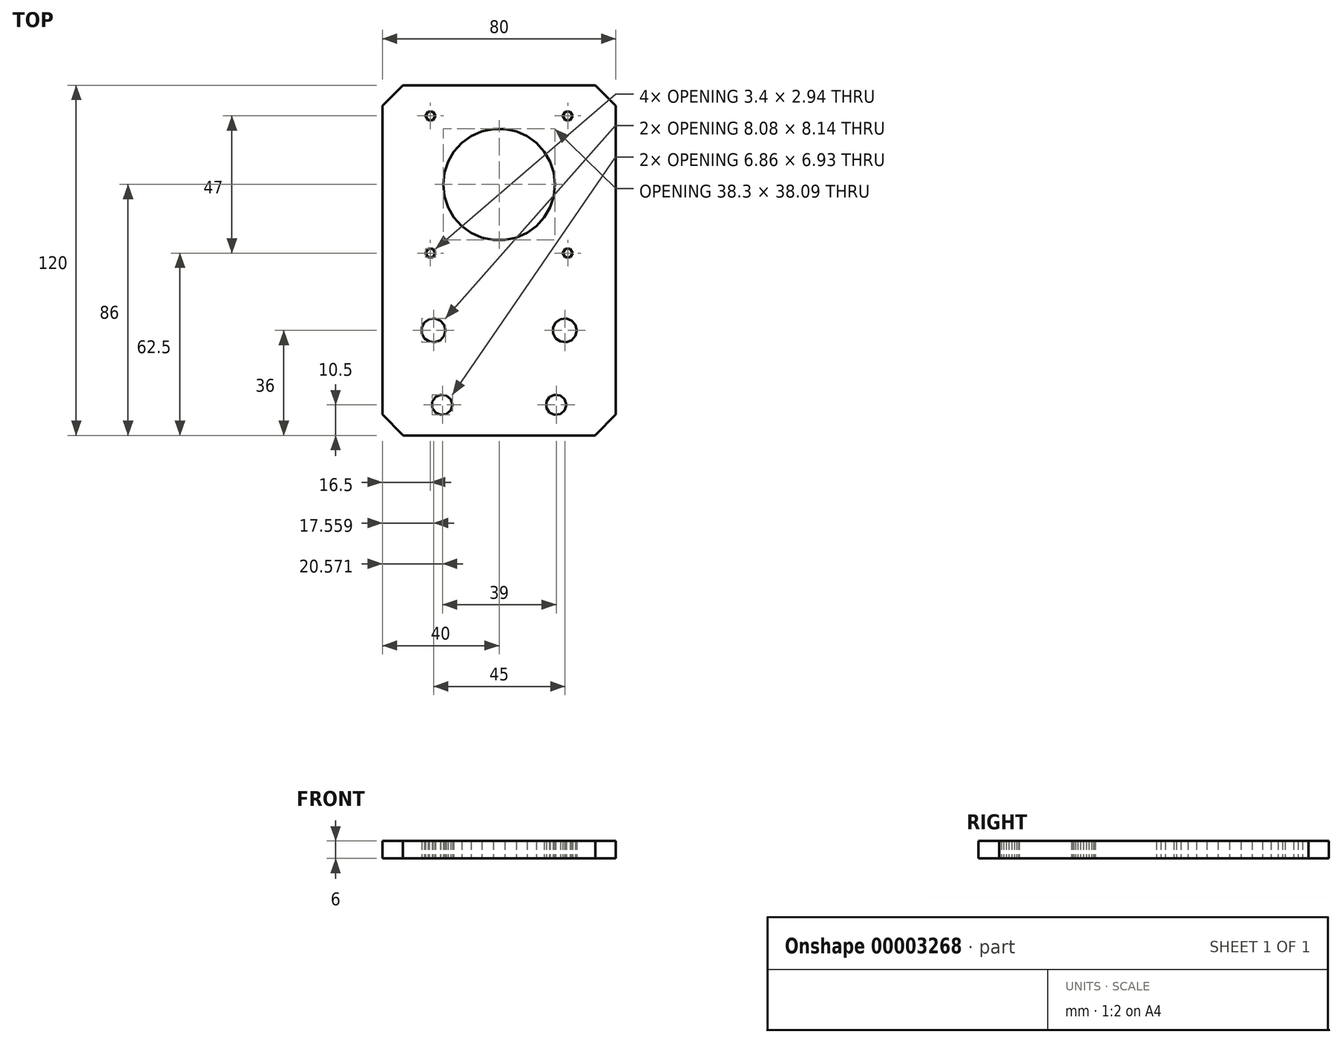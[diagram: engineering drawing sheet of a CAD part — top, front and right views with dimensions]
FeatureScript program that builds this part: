
annotation { "Feature Type Name" : "Feature", "Feature Type Description" : "" }
export const myFeature = defineFeature(function(context is Context, id is Id, definition is map)
    precondition{}
    {
        {
            var Q0;
            Q0=qCreatedBy(makeId("Top.planeOp"),FACE);
            var sketch = newSketch(context, id + "F0", { "sketchPlane" : qUnion([Q0])});
            skLineSegment(sketch, "E0", {"start": v(-40, -52.86) * mm, "end": v(-40, 53) * mm});
            skLineSegment(sketch, "E1", {"start": v(-40, 53) * mm, "end": v(-33, 60) * mm});
            skLineSegment(sketch, "E2", {"start": v(-33, 60) * mm, "end": v(33, 60) * mm});
            skLineSegment(sketch, "E3", {"start": v(33, 60) * mm, "end": v(40, 53) * mm});
            skLineSegment(sketch, "E4", {"start": v(40, 53) * mm, "end": v(40, -52.86) * mm});
            skLineSegment(sketch, "E5", {"start": v(40, -52.86) * mm, "end": v(32.93, -59.93) * mm});
            skLineSegment(sketch, "E6", {"start": v(32.93, -59.93) * mm, "end": v(33, -60) * mm});
            skLineSegment(sketch, "E7", {"start": v(33, -60) * mm, "end": v(-33, -60) * mm});
            skLineSegment(sketch, "E8", {"start": v(-33, -60) * mm, "end": v(-32.93, -59.93) * mm});
            skLineSegment(sketch, "E9", {"start": v(-32.93, -59.93) * mm, "end": v(-40, -52.86) * mm});
            skLineSegment(sketch, "E10", {"start": v(-26.48, -24.98) * mm, "end": v(-26.48, -23.02) * mm});
            skLineSegment(sketch, "E11", {"start": v(-26.48, -23.02) * mm, "end": v(-25.57, -21.28) * mm});
            skLineSegment(sketch, "E12", {"start": v(-25.57, -21.28) * mm, "end": v(-23.95, -20.17) * mm});
            skLineSegment(sketch, "E13", {"start": v(-23.95, -20.17) * mm, "end": v(-22, -19.93) * mm});
            skLineSegment(sketch, "E14", {"start": v(-22, -19.93) * mm, "end": v(-20.17, -20.63) * mm});
            skLineSegment(sketch, "E15", {"start": v(-20.17, -20.63) * mm, "end": v(-18.87, -22.1) * mm});
            skLineSegment(sketch, "E16", {"start": v(-18.87, -22.1) * mm, "end": v(-18.4, -24) * mm});
            skLineSegment(sketch, "E17", {"start": v(-18.4, -24) * mm, "end": v(-18.87, -25.9) * mm});
            skLineSegment(sketch, "E18", {"start": v(-18.87, -25.9) * mm, "end": v(-20.17, -27.37) * mm});
            skLineSegment(sketch, "E19", {"start": v(-20.17, -27.37) * mm, "end": v(-22, -28.07) * mm});
            skLineSegment(sketch, "E20", {"start": v(-22, -28.07) * mm, "end": v(-23.95, -27.83) * mm});
            skLineSegment(sketch, "E21", {"start": v(-23.95, -27.83) * mm, "end": v(-25.57, -26.72) * mm});
            skLineSegment(sketch, "E22", {"start": v(-25.57, -26.72) * mm, "end": v(-26.48, -24.98) * mm});
            skLineSegment(sketch, "E23", {"start": v(-25.2, 2.5) * mm, "end": v(-24.35, 3.97) * mm});
            skLineSegment(sketch, "E24", {"start": v(-24.35, 3.97) * mm, "end": v(-22.65, 3.97) * mm});
            skLineSegment(sketch, "E25", {"start": v(-22.65, 3.97) * mm, "end": v(-21.8, 2.5) * mm});
            skLineSegment(sketch, "E26", {"start": v(-21.8, 2.5) * mm, "end": v(-22.65, 1.03) * mm});
            skLineSegment(sketch, "E27", {"start": v(-22.65, 1.03) * mm, "end": v(-24.35, 1.03) * mm});
            skLineSegment(sketch, "E28", {"start": v(-24.35, 1.03) * mm, "end": v(-25.2, 2.5) * mm});
            skLineSegment(sketch, "E29", {"start": v(-25.2, 49.5) * mm, "end": v(-24.35, 50.97) * mm});
            skLineSegment(sketch, "E30", {"start": v(-24.35, 50.97) * mm, "end": v(-22.65, 50.97) * mm});
            skLineSegment(sketch, "E31", {"start": v(-22.65, 50.97) * mm, "end": v(-21.8, 49.5) * mm});
            skLineSegment(sketch, "E32", {"start": v(-21.8, 49.5) * mm, "end": v(-22.65, 48.03) * mm});
            skLineSegment(sketch, "E33", {"start": v(-22.65, 48.03) * mm, "end": v(-24.35, 48.03) * mm});
            skLineSegment(sketch, "E34", {"start": v(-24.35, 48.03) * mm, "end": v(-25.2, 49.5) * mm});
            skLineSegment(sketch, "E35", {"start": v(-22.86, -50.49) * mm, "end": v(-22.86, -48.51) * mm});
            skLineSegment(sketch, "E36", {"start": v(-22.86, -48.51) * mm, "end": v(-21.8, -46.86) * mm});
            skLineSegment(sketch, "E37", {"start": v(-21.8, -46.86) * mm, "end": v(-20, -46.04) * mm});
            skLineSegment(sketch, "E38", {"start": v(-20, -46.04) * mm, "end": v(-18.05, -46.32) * mm});
            skLineSegment(sketch, "E39", {"start": v(-18.05, -46.32) * mm, "end": v(-16.56, -47.6) * mm});
            skLineSegment(sketch, "E40", {"start": v(-16.56, -47.6) * mm, "end": v(-16, -49.5) * mm});
            skLineSegment(sketch, "E41", {"start": v(-16, -49.5) * mm, "end": v(-16.56, -51.4) * mm});
            skLineSegment(sketch, "E42", {"start": v(-16.56, -51.4) * mm, "end": v(-18.05, -52.68) * mm});
            skLineSegment(sketch, "E43", {"start": v(-18.05, -52.68) * mm, "end": v(-20, -52.96) * mm});
            skLineSegment(sketch, "E44", {"start": v(-20, -52.96) * mm, "end": v(-21.8, -52.15) * mm});
            skLineSegment(sketch, "E45", {"start": v(-21.8, -52.15) * mm, "end": v(-22.86, -50.49) * mm});
            skLineSegment(sketch, "E46", {"start": v(-19.15, 26) * mm, "end": v(-18.73, 29.98) * mm});
            skLineSegment(sketch, "E47", {"start": v(-18.73, 29.98) * mm, "end": v(-17.5, 33.79) * mm});
            skLineSegment(sketch, "E48", {"start": v(-17.5, 33.79) * mm, "end": v(-15.5, 37.26) * mm});
            skLineSegment(sketch, "E49", {"start": v(-15.5, 37.26) * mm, "end": v(-12.81, 40.23) * mm});
            skLineSegment(sketch, "E50", {"start": v(-12.81, 40.23) * mm, "end": v(-9.57, 42.58) * mm});
            skLineSegment(sketch, "E51", {"start": v(-9.57, 42.58) * mm, "end": v(-5.92, 44.21) * mm});
            skLineSegment(sketch, "E52", {"start": v(-5.92, 44.21) * mm, "end": v(-2, 45.05) * mm});
            skLineSegment(sketch, "E53", {"start": v(-2, 45.05) * mm, "end": v(2, 45.05) * mm});
            skLineSegment(sketch, "E54", {"start": v(2, 45.05) * mm, "end": v(5.92, 44.21) * mm});
            skLineSegment(sketch, "E55", {"start": v(5.92, 44.21) * mm, "end": v(9.57, 42.58) * mm});
            skLineSegment(sketch, "E56", {"start": v(9.57, 42.58) * mm, "end": v(12.81, 40.23) * mm});
            skLineSegment(sketch, "E57", {"start": v(12.81, 40.23) * mm, "end": v(15.5, 37.26) * mm});
            skLineSegment(sketch, "E58", {"start": v(15.5, 37.26) * mm, "end": v(17.5, 33.79) * mm});
            skLineSegment(sketch, "E59", {"start": v(17.5, 33.79) * mm, "end": v(18.73, 29.98) * mm});
            skLineSegment(sketch, "E60", {"start": v(18.73, 29.98) * mm, "end": v(19.15, 26) * mm});
            skLineSegment(sketch, "E61", {"start": v(19.15, 26) * mm, "end": v(18.73, 22.02) * mm});
            skLineSegment(sketch, "E62", {"start": v(18.73, 22.02) * mm, "end": v(17.5, 18.21) * mm});
            skLineSegment(sketch, "E63", {"start": v(17.5, 18.21) * mm, "end": v(15.5, 14.74) * mm});
            skLineSegment(sketch, "E64", {"start": v(15.5, 14.74) * mm, "end": v(12.81, 11.77) * mm});
            skLineSegment(sketch, "E65", {"start": v(12.81, 11.77) * mm, "end": v(9.57, 9.42) * mm});
            skLineSegment(sketch, "E66", {"start": v(9.57, 9.42) * mm, "end": v(5.92, 7.79) * mm});
            skLineSegment(sketch, "E67", {"start": v(5.92, 7.79) * mm, "end": v(2, 6.96) * mm});
            skLineSegment(sketch, "E68", {"start": v(2, 6.96) * mm, "end": v(-2, 6.96) * mm});
            skLineSegment(sketch, "E69", {"start": v(-2, 6.96) * mm, "end": v(-5.92, 7.79) * mm});
            skLineSegment(sketch, "E70", {"start": v(-5.92, 7.79) * mm, "end": v(-9.57, 9.42) * mm});
            skLineSegment(sketch, "E71", {"start": v(-9.57, 9.42) * mm, "end": v(-12.81, 11.77) * mm});
            skLineSegment(sketch, "E72", {"start": v(-12.81, 11.77) * mm, "end": v(-15.5, 14.74) * mm});
            skLineSegment(sketch, "E73", {"start": v(-15.5, 14.74) * mm, "end": v(-17.5, 18.21) * mm});
            skLineSegment(sketch, "E74", {"start": v(-17.5, 18.21) * mm, "end": v(-18.73, 22.02) * mm});
            skLineSegment(sketch, "E75", {"start": v(-18.73, 22.02) * mm, "end": v(-19.15, 26) * mm});
            skLineSegment(sketch, "E76", {"start": v(16.14, -50.49) * mm, "end": v(16.14, -48.51) * mm});
            skLineSegment(sketch, "E77", {"start": v(16.14, -48.51) * mm, "end": v(17.2, -46.86) * mm});
            skLineSegment(sketch, "E78", {"start": v(17.2, -46.86) * mm, "end": v(19, -46.04) * mm});
            skLineSegment(sketch, "E79", {"start": v(19, -46.04) * mm, "end": v(20.95, -46.32) * mm});
            skLineSegment(sketch, "E80", {"start": v(20.95, -46.32) * mm, "end": v(22.44, -47.6) * mm});
            skLineSegment(sketch, "E81", {"start": v(22.44, -47.6) * mm, "end": v(23, -49.5) * mm});
            skLineSegment(sketch, "E82", {"start": v(23, -49.5) * mm, "end": v(22.44, -51.4) * mm});
            skLineSegment(sketch, "E83", {"start": v(22.44, -51.4) * mm, "end": v(20.95, -52.68) * mm});
            skLineSegment(sketch, "E84", {"start": v(20.95, -52.68) * mm, "end": v(19, -52.96) * mm});
            skLineSegment(sketch, "E85", {"start": v(19, -52.96) * mm, "end": v(17.2, -52.15) * mm});
            skLineSegment(sketch, "E86", {"start": v(17.2, -52.15) * mm, "end": v(16.14, -50.49) * mm});
            skLineSegment(sketch, "E87", {"start": v(18.52, -24.98) * mm, "end": v(18.52, -23.02) * mm});
            skLineSegment(sketch, "E88", {"start": v(18.52, -23.02) * mm, "end": v(19.43, -21.28) * mm});
            skLineSegment(sketch, "E89", {"start": v(19.43, -21.28) * mm, "end": v(21.05, -20.17) * mm});
            skLineSegment(sketch, "E90", {"start": v(21.05, -20.17) * mm, "end": v(23, -19.93) * mm});
            skLineSegment(sketch, "E91", {"start": v(23, -19.93) * mm, "end": v(24.83, -20.63) * mm});
            skLineSegment(sketch, "E92", {"start": v(24.83, -20.63) * mm, "end": v(26.13, -22.1) * mm});
            skLineSegment(sketch, "E93", {"start": v(26.13, -22.1) * mm, "end": v(26.6, -24) * mm});
            skLineSegment(sketch, "E94", {"start": v(26.6, -24) * mm, "end": v(26.13, -25.9) * mm});
            skLineSegment(sketch, "E95", {"start": v(26.13, -25.9) * mm, "end": v(24.83, -27.37) * mm});
            skLineSegment(sketch, "E96", {"start": v(24.83, -27.37) * mm, "end": v(23, -28.07) * mm});
            skLineSegment(sketch, "E97", {"start": v(23, -28.07) * mm, "end": v(21.05, -27.83) * mm});
            skLineSegment(sketch, "E98", {"start": v(21.05, -27.83) * mm, "end": v(19.43, -26.72) * mm});
            skLineSegment(sketch, "E99", {"start": v(19.43, -26.72) * mm, "end": v(18.52, -24.98) * mm});
            skLineSegment(sketch, "E100", {"start": v(21.8, 2.5) * mm, "end": v(22.65, 3.97) * mm});
            skLineSegment(sketch, "E101", {"start": v(22.65, 3.97) * mm, "end": v(24.35, 3.97) * mm});
            skLineSegment(sketch, "E102", {"start": v(24.35, 3.97) * mm, "end": v(25.2, 2.5) * mm});
            skLineSegment(sketch, "E103", {"start": v(25.2, 2.5) * mm, "end": v(24.35, 1.03) * mm});
            skLineSegment(sketch, "E104", {"start": v(24.35, 1.03) * mm, "end": v(22.65, 1.03) * mm});
            skLineSegment(sketch, "E105", {"start": v(22.65, 1.03) * mm, "end": v(21.8, 2.5) * mm});
            skLineSegment(sketch, "E106", {"start": v(21.8, 49.5) * mm, "end": v(22.65, 50.97) * mm});
            skLineSegment(sketch, "E107", {"start": v(22.65, 50.97) * mm, "end": v(24.35, 50.97) * mm});
            skLineSegment(sketch, "E108", {"start": v(24.35, 50.97) * mm, "end": v(25.2, 49.5) * mm});
            skLineSegment(sketch, "E109", {"start": v(25.2, 49.5) * mm, "end": v(24.35, 48.03) * mm});
            skLineSegment(sketch, "E110", {"start": v(24.35, 48.03) * mm, "end": v(22.65, 48.03) * mm});
            skLineSegment(sketch, "E111", {"start": v(22.65, 48.03) * mm, "end": v(21.8, 49.5) * mm});
            skSolve(sketch);
        }
        {
            var Q0;
            Q0=makeQuery(id+"F0.imprint","IMPRINT",FACE,{"disambiguationData":[TD([[makeQuery(id+"F0.imprint","IMPRINT",EDGE,{"derivedFrom":sQuery(id+"F0.wireOp",EDGE,"E0")}),-1.0]])]});
            extrude(context, id + "F1", {"entities" : qUnion([Q0]), "depth" : 6 * mm});
        }
    });
